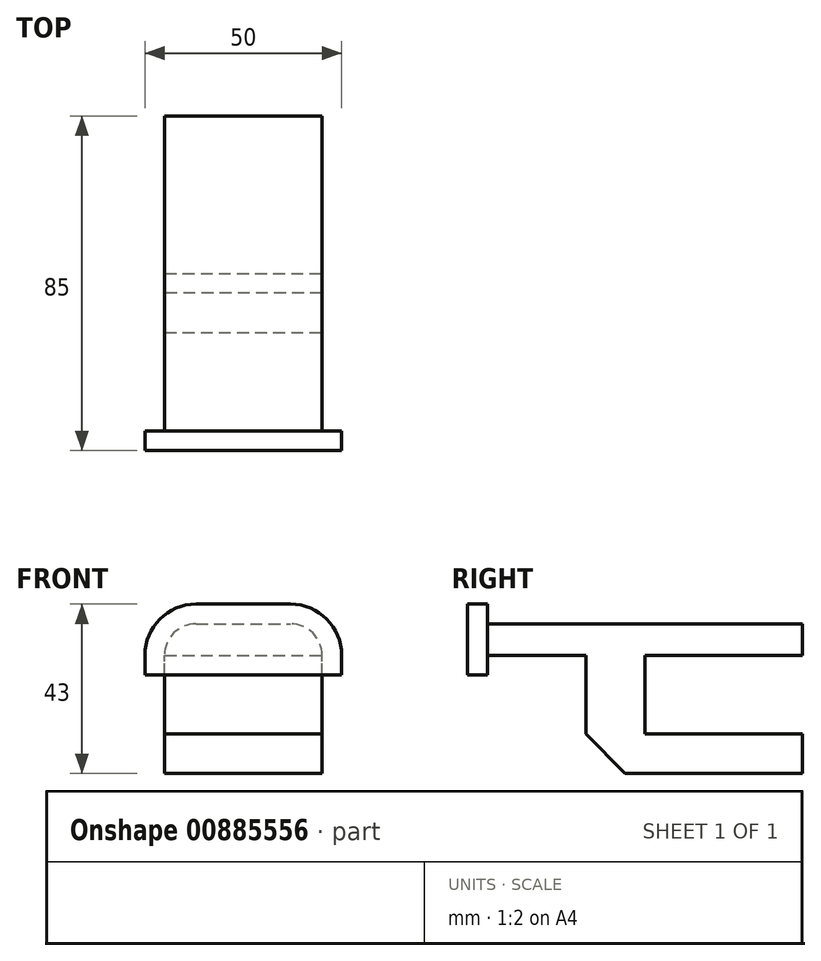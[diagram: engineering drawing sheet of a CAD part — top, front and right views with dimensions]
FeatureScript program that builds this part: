
annotation { "Feature Type Name" : "Feature", "Feature Type Description" : "" }
export const myFeature = defineFeature(function(context is Context, id is Id, definition is map)
    precondition{}
    {
        {
            var Q0;
            Q0=qCreatedBy(makeId("Top.planeOp"),FACE);
            var sketch = newSketch(context, id + "F0", { "sketchPlane" : qUnion([Q0])});
            skLineSegment(sketch, "E0.bottom", {"start": v(-40, -37.9) * mm, "end": v(0, -37.9) * mm});
            skLineSegment(sketch, "E0.top", {"start": v(-40, 42.1) * mm, "end": v(0, 42.1) * mm});
            skLineSegment(sketch, "E0.left", {"start": v(-40, -37.9) * mm, "end": v(-40, 42.1) * mm});
            skLineSegment(sketch, "E0.right", {"start": v(0, -37.9) * mm, "end": v(0, 42.1) * mm});
            skSolve(sketch);
        }
        {
            var Q0;
            Q0=qSketchRegion(id+"F0",true);
            extrude(context, id + "F1", {"entities" : qUnion([Q0]), "depth" : 8 * mm, "offsetDistance" : 25 * mm});
        }
        {
            var Q0;
            Q0=makeQuery(id+"F1.opExtrude","CAP_FACE",FACE,{"disambiguationData":[OSD([sQuery(id+"F0.wireOp",EDGE,"E0.bottom"),sQuery(id+"F0.wireOp",EDGE,"E0.top"),sQuery(id+"F0.wireOp",EDGE,"E0.left"),sQuery(id+"F0.wireOp",EDGE,"E0.right")])],"isStart":true});
            var sketch = newSketch(context, id + "F2", { "sketchPlane" : qUnion([Q0])});
            skLineSegment(sketch, "E1.bottom", {"start": v(-40, 37.9) * mm, "end": v(0, 37.9) * mm});
            skLineSegment(sketch, "E1.top", {"start": v(-40, -2.1) * mm, "end": v(0, -2.1) * mm});
            skLineSegment(sketch, "E1.left", {"start": v(-40, 37.9) * mm, "end": v(-40, -2.1) * mm});
            skLineSegment(sketch, "E1.right", {"start": v(0, 37.9) * mm, "end": v(0, -2.1) * mm});
            skLineSegment(sketch, "E2.top", {"start": v(-40, 12.9) * mm, "end": v(0, 12.9) * mm});
            skLineSegment(sketch, "E2.left", {"start": v(-40, -2.1) * mm, "end": v(-40, 12.9) * mm});
            skLineSegment(sketch, "E2.right", {"start": v(0, -2.1) * mm, "end": v(0, 12.9) * mm});
            skSolve(sketch);
        }
        {
            var Q0;
            {var subQ0=sQuery(id+"F2.wireOp",EDGE,"E1.top");Q0=makeQuery(id+"F2.imprint","IMPRINT",FACE,{"disambiguationData":[TD([[makeQuery(id+"F2.imprint","IMPRINT",EDGE,{"derivedFrom":subQ0}),1.0]])]});}
            extrude(context, id + "F3", {"entities" : qUnion([Q0]), "operationType" : NewBodyOperationType.ADD, "depth" : 30 * mm, "offsetDistance" : 25 * mm});
        }
        {
            var Q0;
            Q0=makeQuery(id+"F3.opExtrude","SWEPT_FACE",FACE,{"disambiguationData":[OSD([sQuery(id+"F2.wireOp",EDGE,"E1.top")])]});
            var sketch = newSketch(context, id + "F4", { "sketchPlane" : qUnion([Q0])});
            skLineSegment(sketch, "E3.bottom", {"start": v(0, -30) * mm, "end": v(40, -30) * mm});
            skLineSegment(sketch, "E3.top", {"start": v(0, -20) * mm, "end": v(40, -20) * mm});
            skLineSegment(sketch, "E3.left", {"start": v(0, -30) * mm, "end": v(0, -20) * mm});
            skLineSegment(sketch, "E3.right", {"start": v(40, -30) * mm, "end": v(40, -20) * mm});
            skSolve(sketch);
        }
        {
            var Q0;
            Q0=qSketchRegion(id+"F4",true);
            extrude(context, id + "F5", {"entities" : qUnion([Q0]), "operationType" : NewBodyOperationType.ADD, "depth" : 40 * mm, "offsetDistance" : 25 * mm});
        }
        {
            var Q0;
            Q0=makeQuery(id+"F1.opExtrude","CAP_EDGE",EDGE,{"disambiguationData":[OSD([sQuery(id+"F0.wireOp",EDGE,"E0.right")])],"isStart":false});
            var Q1;
            Q1=makeQuery(id+"F1.opExtrude","CAP_EDGE",EDGE,{"disambiguationData":[OSD([sQuery(id+"F0.wireOp",EDGE,"E0.left")])],"isStart":false});
            fillet(context, id + "F6", {"entities" : qUnion([Q0, Q1]), "radius" : 8 * mm, "tangentPropagation" : true, "allowEdgeOverflow" : false});
        }
        {
            var Q0;
            Q0=makeQuery(id+"F3.opExtrude","CAP_EDGE",EDGE,{"disambiguationData":[OSD([sQuery(id+"F2.wireOp",EDGE,"E2.top")])],"isStart":false});
            chamfer(context, id + "F7", {"entities" : qUnion([Q0]), "chamferType" : ChamferType.TWO_OFFSETS, "width1" : 10 * mm, "oppositeDirection" : true, "width2" : 10 * mm, "tangentPropagation" : true});
        }
        {
            var Q0;
            Q0=makeQuery(id+"F1.opExtrude","SWEPT_FACE",FACE,{"disambiguationData":[OSD([sQuery(id+"F0.wireOp",EDGE,"E0.bottom")])]});
            var sketch = newSketch(context, id + "F8", { "sketchPlane" : qUnion([Q0])});
            skArc(sketch, "E4.0", {"start": v(4, -5) * mm, "mid": v(2.82, 7.21) * mm, "end": v(-8, 13) * mm});
            skLineSegment(sketch, "E4.1", {"start": v(-44, -5) * mm, "end": v(4, -5) * mm});
            skArc(sketch, "E4.2", {"start": v(-32, 13) * mm, "mid": v(-42.82, 7.21) * mm, "end": v(-44, -5) * mm});
            skLineSegment(sketch, "E5", {"start": v(-32, 13) * mm, "end": v(-8, 13) * mm});
            skSolve(sketch);
        }
        {
            var Q0;
            Q0 = qSketchRegion(id + "F8", true);
            extrude(context, id + "F9", {"entities" : qUnion([Q0]), "operationType" : NewBodyOperationType.ADD, "depth" : 5 * mm, "offsetDistance" : 25 * mm});
        }
        {
            var Q0;
            Q0=makeQuery(id+"F9.opExtrude","SWEPT_FACE",FACE,{"disambiguationData":[OSD([sQuery(id+"F8.wireOp",EDGE,"E4.1")])]});
            var sketch = newSketch(context, id + "F10", { "sketchPlane" : qUnion([Q0])});
            skLineSegment(sketch, "E6.bottom", {"start": v(-44, 37.9) * mm, "end": v(4, 37.9) * mm});
            skLineSegment(sketch, "E6.top", {"start": v(-44, 42.9) * mm, "end": v(4, 42.9) * mm});
            skLineSegment(sketch, "E6.left", {"start": v(-44, 37.9) * mm, "end": v(-44, 42.9) * mm});
            skLineSegment(sketch, "E6.right", {"start": v(4, 37.9) * mm, "end": v(4, 42.9) * mm});
            skLineSegment(sketch, "E7.bottom", {"start": v(4, 42.9) * mm, "end": v(5, 42.9) * mm});
            skLineSegment(sketch, "E7.top", {"start": v(4, 37.9) * mm, "end": v(5, 37.9) * mm});
            skLineSegment(sketch, "E7.left", {"start": v(4, 42.9) * mm, "end": v(4, 37.9) * mm});
            skLineSegment(sketch, "E7.right", {"start": v(5, 42.9) * mm, "end": v(5, 37.9) * mm});
            skLineSegment(sketch, "E8.bottom", {"start": v(-44, 42.9) * mm, "end": v(-45, 42.9) * mm});
            skLineSegment(sketch, "E8.top", {"start": v(-44, 37.9) * mm, "end": v(-45, 37.9) * mm});
            skLineSegment(sketch, "E8.left", {"start": v(-44, 42.9) * mm, "end": v(-44, 37.9) * mm});
            skLineSegment(sketch, "E8.right", {"start": v(-45, 42.9) * mm, "end": v(-45, 37.9) * mm});
            skSolve(sketch);
        }
        {
            var Q0;
            Q0 = qSketchRegion(id + "F10", true);
            extrude(context, id + "F11", {"entities" : qUnion([Q0]), "operationType" : NewBodyOperationType.ADD, "oppositeDirection" : true, "depth" : 5 * mm, "offsetDistance" : 25 * mm});
        }
    });
